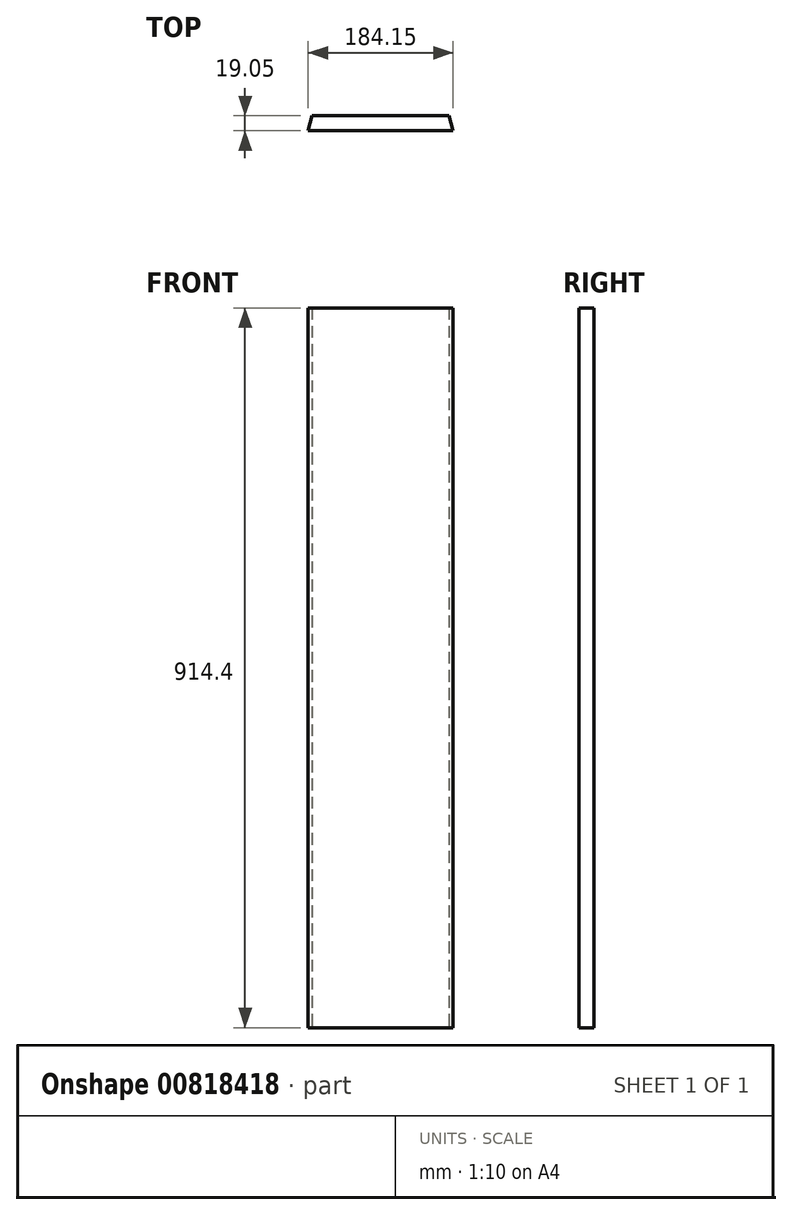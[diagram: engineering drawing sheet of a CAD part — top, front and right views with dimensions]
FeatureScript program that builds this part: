
annotation { "Feature Type Name" : "Feature", "Feature Type Description" : "" }
export const myFeature = defineFeature(function(context is Context, id is Id, definition is map)
    precondition{}
    {
        {
            var Q0;
            Q0=qCreatedBy(makeId("Top.planeOp"),FACE);
            var sketch = newSketch(context, id + "F0", { "sketchPlane" : qUnion([Q0])});
            skLineSegment(sketch, "E0", {"start": v(0, 0) * mm, "end": v(184.15, 0) * mm});
            skLineSegment(sketch, "E1", {"start": v(184.15, 0) * mm, "end": v(179.05, 19.05) * mm});
            skLineSegment(sketch, "E2", {"start": v(179.05, 19.05) * mm, "end": v(5.1, 19.05) * mm});
            skLineSegment(sketch, "E3", {"start": v(5.1, 19.05) * mm, "end": v(0, 0) * mm});
            skSolve(sketch);
        }
        {
            var Q0;
            Q0=makeQuery(id+"F0.imprint","IMPRINT",FACE,{"disambiguationData":[TD([[makeQuery(id+"F0.imprint","IMPRINT",EDGE,{"derivedFrom":sQuery(id+"F0.wireOp",EDGE,"E0")}),1.0]])]});
            extrude(context, id + "F1", {"entities" : qUnion([Q0]), "depth" : 914.4 * mm, "offsetDistance" : 25.4 * mm});
        }
    });
